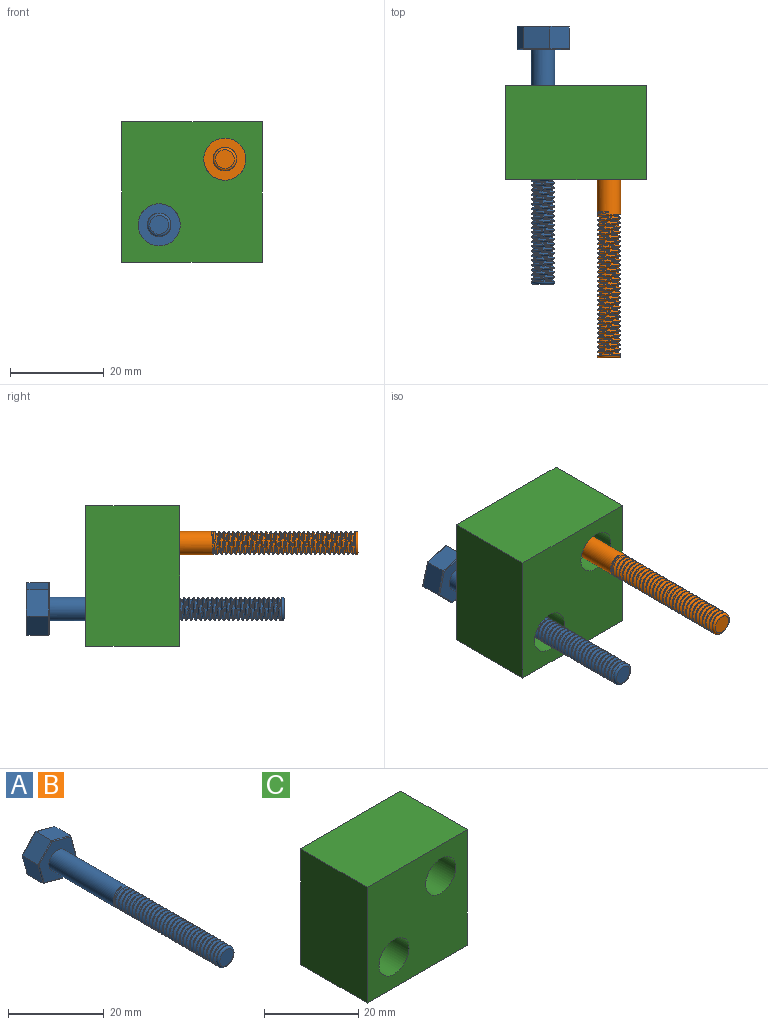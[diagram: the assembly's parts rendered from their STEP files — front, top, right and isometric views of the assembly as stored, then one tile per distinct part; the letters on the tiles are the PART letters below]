
ASSEMBLY  parts=3 mates=2
PART A: 61 faces, bbox 11.4x55.3x11.4 mm
  f0: plane 5.59x4.6mm, normal (-0.25,0,-0.97), area 26.6mm2, adj f1,f5,f51,f57
  f1: plane 4.6x4.11mm, normal (0.71,0,-0.7), area 26.6mm2, adj f0,f2,f49,f55
  f2: plane 5.57x4.6mm, normal (0.96,0,0.27), area 26.6mm2, adj f1,f3,f50,f56
  f3: plane 5.59x4.6mm, normal (0.25,0,0.97), area 26.6mm2, adj f2,f4,f52,f58
  f4: plane 4.6x4.11mm, normal (-0.71,0,0.7), area 26.6mm2, adj f3,f5,f54,f60
  f5: plane 5.57x4.6mm, normal (-0.96,0,-0.27), area 26.6mm2, adj f0,f4,f53,f59
  f6: plane 10.73x10.69mm, normal (0,-1,0), area 60.2mm2, adj f8,f55,f56,f57,f58,f59,f60
  f7: plane 10.73x10.69mm, normal (0,1,0), area 79.8mm2, adj f49,f50,f51,f52,f53,f54
  f8: cylinder r=2.5mm len=20.5mm, axis (0,1,0), area 305mm2, adj f6,f9,f41,f42,f43,f46
  f9: cylinder r=2.5mm len=5mm, axis (0,1,0), area 2mm2, adj f8,f10,f45,f46
  f10: cylinder r=2.5mm len=5mm, axis (0,1,0), area 2mm2, adj f9,f11,f45,f46
  f11: cylinder r=2.5mm len=5mm, axis (0,1,0), area 2mm2, adj f10,f12,f45,f46
  f12: cylinder r=2.5mm len=5mm, axis (0,1,0), area 2mm2, adj f11,f13,f45,f46
  f13: cylinder r=2.5mm len=5mm, axis (0,1,0), area 2mm2, adj f12,f14,f45,f46
  f14: cylinder r=2.5mm len=5mm, axis (0,1,0), area 2mm2, adj f13,f15,f45,f46
  f15: cylinder r=2.5mm len=5mm, axis (0,1,0), area 2mm2, adj f14,f16,f45,f46
  f16: cylinder r=2.5mm len=5mm, axis (0,1,0), area 2mm2, adj f15,f17,f45,f46
  f17: cylinder r=2.5mm len=5mm, axis (0,1,0), area 2mm2, adj f16,f18,f45,f46
  f18: cylinder r=2.5mm len=5mm, axis (0,1,0), area 2mm2, adj f17,f19,f45,f46
  f19: cylinder r=2.5mm len=5mm, axis (0,1,0), area 2mm2, adj f18,f20,f45,f46
  f20: cylinder r=2.5mm len=5mm, axis (0,1,0), area 2mm2, adj f19,f21,f45,f46
  f21: cylinder r=2.5mm len=5mm, axis (0,1,0), area 2mm2, adj f20,f22,f45,f46
  f22: cylinder r=2.5mm len=5mm, axis (0,1,0), area 2mm2, adj f21,f23,f45,f46
  f23: cylinder r=2.5mm len=5mm, axis (0,1,0), area 2mm2, adj f22,f24,f45,f46
  f24: cylinder r=2.5mm len=5mm, axis (0,1,0), area 2mm2, adj f23,f25,f45,f46
  f25: cylinder r=2.5mm len=5mm, axis (0,1,0), area 2mm2, adj f24,f26,f45,f46
  f26: cylinder r=2.5mm len=5mm, axis (0,1,0), area 2mm2, adj f25,f27,f45,f46
  f27: cylinder r=2.5mm len=5mm, axis (0,1,0), area 2mm2, adj f26,f28,f45,f46
  f28: cylinder r=2.5mm len=5mm, axis (0,1,0), area 2mm2, adj f27,f29,f45,f46
  f29: cylinder r=2.5mm len=5mm, axis (0,1,0), area 2mm2, adj f28,f30,f45,f46
  f30: cylinder r=2.5mm len=5mm, axis (0,1,0), area 2mm2, adj f29,f31,f45,f46
  f31: cylinder r=2.5mm len=5mm, axis (0,1,0), area 2mm2, adj f30,f32,f45,f46
  f32: cylinder r=2.5mm len=5mm, axis (0,1,0), area 2mm2, adj f31,f33,f45,f46
  f33: cylinder r=2.5mm len=5mm, axis (0,1,0), area 2mm2, adj f32,f34,f45,f46
  f34: cylinder r=2.5mm len=5mm, axis (0,1,0), area 2mm2, adj f33,f35,f45,f46
  f35: cylinder r=2.5mm len=5mm, axis (0,1,0), area 2mm2, adj f34,f36,f45,f46
  f36: cylinder r=2.5mm len=5mm, axis (0,1,0), area 2mm2, adj f35,f37,f45,f46
  f37: cylinder r=2.5mm len=5mm, axis (0,1,0), area 2mm2, adj f36,f38,f45,f46
  f38: cylinder r=2.5mm len=1.75mm, axis (0,1,0), area 0.1mm2, adj f37,f40,f45
  f39: plane 4x4mm, normal (0,-1,0), area 12.6mm2, adj f40
  f40: torus R=2mm, axis (0,-1,0), area 11.4mm2, adj f38,f39,f48
  f41: plane 0.3x0.1mm, normal (-1,0.01,0.01), area 0mm2, adj f8,f42,f43,f47
  f42: bspline ~5.77x5.55mm, area 4.9mm2, adj f8,f41,f45,f47
  f43: bspline ~5.77x5.55mm, area 4.9mm2, adj f8,f41,f46,f47
  f44: bspline ~30.08x4.52mm, area 100.3mm2, adj f45,f46,f47,f48
  f45: bspline ~29.81x5.77mm, area 256.8mm2, adj f9,f10,f11,f12,f13,f14,f15,f16
  f46: bspline ~30.31x5.77mm, area 262mm2, adj f8,f9,f10,f11,f12,f13,f14,f15
  f47: bspline ~4.69x4.46mm, area 3.8mm2, adj f41,f42,f43,f44
  f48: plane 5.27x5.27mm, normal (0,1,0), area 4.5mm2, adj f40,f44,f45,f46
  f49: cylinder r=0.2mm len=4.25mm, axis (0.7,0,0.71), area 1.8mm2, adj f1,f7,f50,f51
  f50: cylinder r=0.2mm len=5.62mm, axis (-0.27,0,0.96), area 1.8mm2, adj f2,f7,f49,f52
  f51: cylinder r=0.2mm len=5.64mm, axis (0.97,0,-0.25), area 1.8mm2, adj f0,f7,f49,f53
  f52: cylinder r=0.2mm len=5.64mm, axis (-0.97,0,0.25), area 1.8mm2, adj f3,f7,f50,f54
  f53: cylinder r=0.2mm len=5.62mm, axis (0.27,0,-0.96), area 1.8mm2, adj f5,f7,f51,f54
  f54: cylinder r=0.2mm len=4.25mm, axis (-0.7,0,-0.71), area 1.8mm2, adj f4,f7,f52,f53
  f55: cylinder r=0.2mm len=4.25mm, axis (-0.7,0,-0.71), area 1.8mm2, adj f1,f6,f56,f57
  f56: cylinder r=0.2mm len=5.62mm, axis (0.27,0,-0.96), area 1.8mm2, adj f2,f6,f55,f58
  f57: cylinder r=0.2mm len=5.64mm, axis (-0.97,0,0.25), area 1.8mm2, adj f0,f6,f55,f59
  f58: cylinder r=0.2mm len=5.64mm, axis (0.97,0,-0.25), area 1.8mm2, adj f3,f6,f56,f60
  f59: cylinder r=0.2mm len=5.62mm, axis (-0.27,0,0.96), area 1.8mm2, adj f5,f6,f57,f60
  f60: cylinder r=0.2mm len=4.25mm, axis (0.7,0,0.71), area 1.8mm2, adj f4,f6,f58,f59
PART B: same geometry as A
PART C: 12 faces, bbox 30x20x30 mm
  f0: plane 30x20mm, normal (0,0,1), area 600mm2, adj f1,f3,f4,f5
  f1: plane 30x20mm, normal (-1,0,0), area 600mm2, adj f0,f2,f4,f5
  f2: plane 30x20mm, normal (0,0,-1), area 600mm2, adj f1,f3,f4,f5
  f3: plane 30x20mm, normal (1,0,0), area 600mm2, adj f0,f2,f4,f5
  f4: plane 30x30mm, normal (0,-1,0), area 772.8mm2, adj f0,f1,f2,f3,f6,f9
  f5: plane 30x30mm, normal (0,1,0), area 581mm2, adj f0,f1,f2,f3,f8,f11
  f6: cylinder r=4.5mm len=12mm, axis (0,1,0), area 339.3mm2, adj f4,f7
  f7: plane 14.25x14.25mm, normal (0,1,0), area 95.9mm2, adj f6,f8
  f8: cylinder r=7.12mm len=14.25mm, axis (0,1,0), area 358.1mm2, adj f5,f7
  f9: cylinder r=4.5mm len=12mm, axis (0,1,0), area 339.3mm2, adj f4,f10
  f10: plane 14.25x14.25mm, normal (0,1,0), area 95.9mm2, adj f9,f11
  f11: cylinder r=7.12mm len=14.25mm, axis (0,1,0), area 358.1mm2, adj f5,f10
PLACE A rot(axis=(0,1,0),90deg) t=(0.11,-96.09,20.77)mm
PLACE B rot(axis=(-0.4,-0.91,-0.07),0deg) t=(14.11,-111.81,34.77)mm
PLACE C rot(axis=(-0.4,-0.91,-0.07),0deg) t=(-29.14,-108.81,10.11)mm
MATE slider A.f8 <-> C.f9  axis (0,-1,0) through (0.11,-151.09,20.77)mm
MATE fastened B.f8 <-> C.f6  axis (0,-1,0) through (14.11,-116.81,34.77)mm
